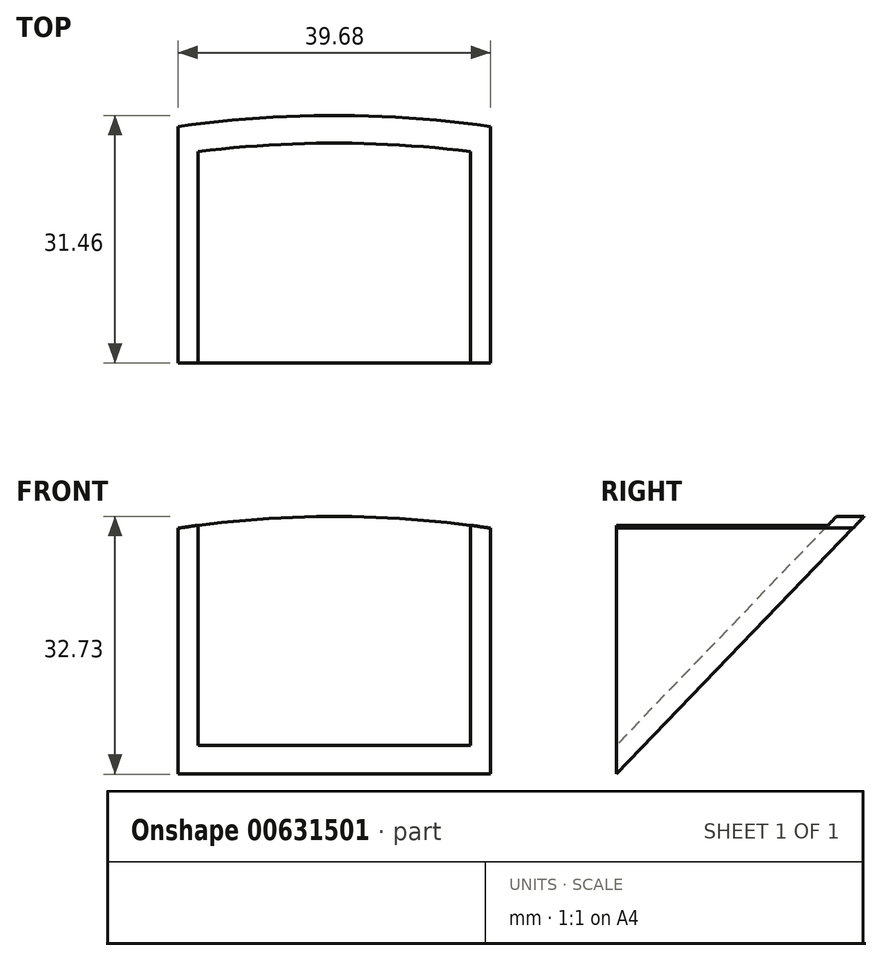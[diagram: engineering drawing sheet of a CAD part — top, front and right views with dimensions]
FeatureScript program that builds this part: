
annotation { "Feature Type Name" : "Feature", "Feature Type Description" : "" }
export const myFeature = defineFeature(function(context is Context, id is Id, definition is map)
    precondition{}
    {
        {
            var Q0;
            Q0=qCreatedBy(makeId("Right.planeOp"),FACE);
            var sketch = newSketch(context, id + "F0", { "sketchPlane" : qUnion([Q0])});
            skLineSegment(sketch, "E0", {"start": v(0, 0) * mm, "end": v(0, 32.8) * mm});
            skLineSegment(sketch, "E1", {"start": v(0, 32.8) * mm, "end": v(31.54, 32.8) * mm});
            skLineSegment(sketch, "E2", {"start": v(31.54, 32.8) * mm, "end": v(0, 0) * mm});
            skLineSegment(sketch, "E3", {"start": v(0, 0) * mm, "end": v(0, -3.67) * mm});
            skLineSegment(sketch, "E4", {"start": v(0, -3.67) * mm, "end": v(35.06, 32.8) * mm});
            skLineSegment(sketch, "E5", {"start": v(35.06, 32.8) * mm, "end": v(31.54, 32.8) * mm});
            skSolve(sketch);
        }
        {
            var Q0;
            Q0=makeQuery(id+"F0.imprint","IMPRINT",FACE,{"disambiguationData":[TD([[makeQuery(id+"F0.imprint","IMPRINT",EDGE,{"derivedFrom":sQuery(id+"F0.wireOp",EDGE,"E2")}),1.0]])]});
            extrude(context, id + "F1", {"entities" : qUnion([Q0]), "depth" : 19.84 * mm, "offsetDistance" : 25.4 * mm, "hasSecondDirection" : true, "secondDirectionOppositeDirection" : true, "secondDirectionDepth" : 19.84 * mm});
        }
        {
            var Q0;
            Q0=makeQuery(id+"F0.imprint","IMPRINT",FACE,{"disambiguationData":[TD([[makeQuery(id+"F0.imprint","IMPRINT",EDGE,{"derivedFrom":sQuery(id+"F0.wireOp",EDGE,"E0")}),-1.0]])]});
            extrude(context, id + "F2", {"entities" : qUnion([Q0]), "operationType" : NewBodyOperationType.ADD, "depth" : 19.84 * mm, "offsetDistance" : 25.4 * mm, "hasSecondDirection" : true, "secondDirectionOppositeDirection" : false, "secondDirectionDepth" : 17.3 * mm});
        }
        {
            var Q0;
            Q0=makeQuery(id+"F0.imprint","IMPRINT",FACE,{"disambiguationData":[TD([[makeQuery(id+"F0.imprint","IMPRINT",EDGE,{"derivedFrom":sQuery(id+"F0.wireOp",EDGE,"E0")}),-1.0]])]});
            extrude(context, id + "F3", {"entities" : qUnion([Q0]), "operationType" : NewBodyOperationType.ADD, "oppositeDirection" : true, "depth" : 19.84 * mm, "offsetDistance" : 25.4 * mm, "hasSecondDirection" : true, "secondDirectionOppositeDirection" : true, "secondDirectionDepth" : 17.3 * mm});
        }
        {
            var Q0;
            Q0=qCreatedBy(makeId("Front.planeOp"),FACE);
            var sketch = newSketch(context, id + "F4", { "sketchPlane" : qUnion([Q0])});
            skLineSegment(sketch, "E6", {"start": v(0, 0) * mm, "end": v(0, 29.06) * mm, "construction": true});
            skLineSegment(sketch, "E7", {"start": v(0, 0) * mm, "end": v(0, -104.3) * mm, "construction": true});
            skCircle(sketch, "E8", {"center": v(0, -104.3) * mm, "radius": 133.35 * mm});
            skCircle(sketch, "E9", {"center": v(0, -104.3) * mm, "radius": 159.25 * mm});
            skSolve(sketch);
        }
        {
            var Q0;
            Q0 = qSketchRegion(id + "F4", true);
            extrude(context, id + "F5", {"entities" : qUnion([Q0]), "operationType" : NewBodyOperationType.REMOVE, "oppositeDirection" : true, "depth" : 127 * mm, "offsetDistance" : 25.4 * mm});
        }
    });
